# Revit family: Zumtobel LINCOR D-DI
name_source: partatom
category: Lighting Fixtures
revit_build: Autodesk Revit 2014 (Build: 20140709_2115(x64)
units: mm (PartAtom-declared; Revit-internal decimal feet)

## types (2) — shared parameters
Apparent Load = 45 VA
Assembly Code = D5020200
Color Filter = 16777215
Description = Pendant LED luminaire - darklight optic
Dimming Lamp Color Temperature Shift = <None>
Emit Shape Visible in Rendering = No
Emit from Rectangle Length = 53 mm  [stored 0.173885 ft]
Height = 65 mm  [stored 0.213255 ft]
Lamp = LED
Manufacturer = Zumtobel Lighting
Tilt Angle = 90.00°
URL = http://www.zumtobel.com
Voltage = 230 V
Width = 63 mm  [stored 0.206693 ft]
zero-valued in all types: Default Elevation

## per-type parameters (varying)
| type | Cell 1209 | Cell 2407 | Emit from Rectangle Width | Length | Model | Photometric Web File | Suspension Distance |
| LINCOR DI D LED5000-840 LDE ASQ1 SR | Yes | No | 1199 mm  [stored 3.93373 ft] | 1209 mm  [stored 3.96654 ft] | 42184416 | 42184416_(STD).IES | 1150 mm  [stored 3.77297 ft] |
| LINCOR DI D LED10000-840 LDE ASQ1 SR | No | Yes | 2397 mm  [stored 7.86417 ft] | 2407 mm  [stored 7.89698 ft] | 42184418 | 42184418_(STD).IES | 2300 mm  [stored 7.54593 ft] |

note: [stored X ft] marks values corroborated as IEEE doubles in the binary element streams (Revit-internal decimal feet)

## geometry (parser evidence)
native form markers: Sweep x3
no freeform markers — native parametric forms only
